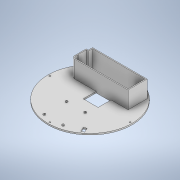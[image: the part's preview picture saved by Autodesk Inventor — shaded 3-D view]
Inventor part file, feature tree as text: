
AUTODESK INVENTOR PART (.ipt)
format: ipt  version: 2021 (Build 250183000, 183)  size: 199,168 bytes
history: native  units: mm
features: extrude x7, other x2, hole x1, pattern_circular x1
ambient origin geometry x8: Origin, YZ Plane, XZ Plane, XY Plane, X Axis, Y Axis, Z Axis, Center Point
bodies: Volumenkörper1 (feature_tree)
feature tree (11):
  other  "00_Mastersketch.ipt"
  extrude  "Extrusion1"  Depth=10.0mm
  extrude  "Extrusion2"  Depth=3.6mm TaperAngle=0.0deg
  hole  "Bohrung1"  [1 undecoded]
  pattern_circular  "Runde Anordnung1"  [2 undecoded]
  extrude  "Extrusion5"  Depth=40.0mm TaperAngle=360.0deg
  extrude  "Extrusion6"  Depth=0.1mm
  extrude  "Extrusion7"  TaperAngle=0.0deg  [1 undecoded]
  extrude  "Extrusion8"  Depth=1.6mm TaperAngle=0.0deg
  extrude  "Extrusion9"  TaperAngle=0.0deg  [1 undecoded]
  other  "03_caseTopSketch"
note: 5 required parameter values undecoded (feature->parameter linkage not recoverable at this tier; creation-order binding heuristic only, values carry confidence <= 0.55)
